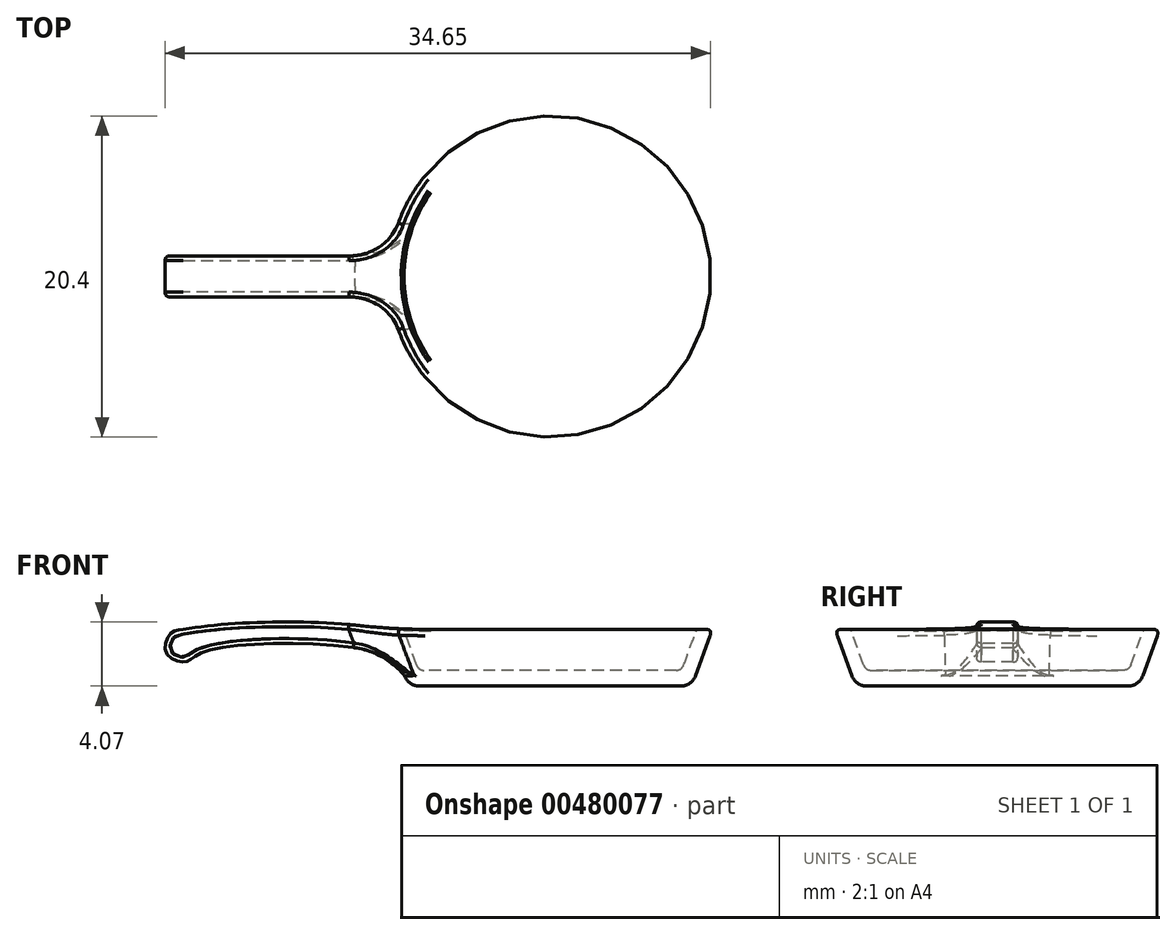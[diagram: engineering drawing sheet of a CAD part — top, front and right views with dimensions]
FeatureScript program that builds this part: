
annotation { "Feature Type Name" : "Feature", "Feature Type Description" : "" }
export const myFeature = defineFeature(function(context is Context, id is Id, definition is map)
    precondition{}
    {
        {
            var Q0;
            Q0=qCreatedBy(makeId("Top.planeOp"),FACE);
            var sketch = newSketch(context, id + "F0", { "sketchPlane" : qUnion([Q0])});
            skCircle(sketch, "E0", {"center": v(0, 0) * mm, "radius": 9 * mm});
            skSolve(sketch);
        }
        {
            var Q0;
            Q0 = qSketchRegion(id + "F0", true);
            extrude(context, id + "F1", {"entities" : qUnion([Q0]), "depth" : 1 * mm});
        }
        {
            var Q0;
            Q0=qCreatedBy(makeId("Front.planeOp"),FACE);
            var sketch = newSketch(context, id + "F2", { "sketchPlane" : qUnion([Q0])});
            skLineSegment(sketch, "E1.0.0", {"start": v(-8, 0) * mm, "end": v(-9, 0) * mm});
            skLineSegment(sketch, "E2", {"start": v(-9, 0) * mm, "end": v(-10.31, 3.6) * mm});
            skLineSegment(sketch, "E3", {"start": v(-10.31, 3.6) * mm, "end": v(-9.31, 3.6) * mm});
            skLineSegment(sketch, "E4", {"start": v(-9.31, 3.6) * mm, "end": v(-8, 0) * mm});
            skPoint(sketch, "E5.orphan", {"position": v(9, 0) * mm});
            skSolve(sketch);
        }
        {
            var Q0;
            Q0=makeQuery(id+"F2.imprint","IMPRINT",FACE,{"disambiguationData":[TD([[makeQuery(id+"F2.imprint","IMPRINT",EDGE,{"derivedFrom":sQuery(id+"F2.wireOp",EDGE,"E1.0.0")}),-1.0]])]});
            var Q1;
            Q1=makeQuery(id+"F1.opExtrude","CAP_EDGE",EDGE,{"disambiguationData":[OSD([sQuery(id+"F0.wireOp",EDGE,"E0")])],"isStart":true});
            revolve(context, id + "F3", {"operationType" : NewBodyOperationType.ADD, "entities" : qUnion([Q0]), "axis" : qUnion([Q1]), "revolveType" : RevolveType.FULL});
        }
        {
            var Q0;
            Q0=makeQuery(id+"F3.boolean.opBoolean","MERGE",EDGE,{"derivedFrom":[makeQuery(id+"F1.opExtrude","CAP_EDGE",EDGE,{"disambiguationData":[OSD([sQuery(id+"F0.wireOp",EDGE,"E0")])],"isStart":true}),makeQuery(id+"F3.opRevolve","SWEPT_EDGE",EDGE,{"disambiguationData":[OSD([sQuery(id+"F2.wireOp",EDGE,"E1.0.0"),sQuery(id+"F2.wireOp",EDGE,"E2")])]})]});
            fillet(context, id + "F4", {"entities" : qUnion([Q0]), "radius" : 1 * mm, "tangentPropagation" : true, "allowEdgeOverflow" : false});
        }
        {
            var Q0;
            Q0=makeQuery(id+"F3.boolean.opBoolean","INTERSECT",EDGE,{"derivedFrom":[makeQuery(id+"F1.opExtrude","CAP_FACE",FACE,{"disambiguationData":[OSD([sQuery(id+"F0.wireOp",EDGE,"E0")])],"isStart":false}),makeQuery(id+"F3.opRevolve","SWEPT_FACE",FACE,{"disambiguationData":[OSD([sQuery(id+"F2.wireOp",EDGE,"E4")])]})]});
            fillet(context, id + "F5", {"entities" : qUnion([Q0]), "radius" : .5 * mm, "tangentPropagation" : true, "allowEdgeOverflow" : false});
        }
        {
            var Q0;
            Q0=qCreatedBy(makeId("Front.planeOp"),FACE);
            var sketch = newSketch(context, id + "F6", { "sketchPlane" : qUnion([Q0])});
            skLineSegment(sketch, "E6.0", {"start": v(-9.44, 3.6) * mm, "end": v(-10.31, 3.6) * mm});
            skFitSpline(sketch, "E7", {"points": [v(-10.31, 3.6) * mm, v(-23.31, 3.6) * mm], "startDerivative": vector(-11.8, 2) * mm, "endDerivative": vector(-10.24, -1.77) * mm});
            skLineSegment(sketch, "E8", {"start": v(9.24, 0.66) * mm, "end": v(10.31, 3.6) * mm});
            skFitSpline(sketch, "E9", {"points": [v(-9.24, 1.7) * mm, v(-22.07, 2.14) * mm, v(-23.2, 1.53) * mm, v(-24.37, 2.1) * mm, v(-24.1, 3.34) * mm, v(-23.31, 3.6) * mm], "startDerivative": vector(-23.26, 8.79) * mm, "endDerivative": vector(7.3, 1.26) * mm});
            skLineSegment(sketch, "E10", {"start": v(-9.24, 1.7) * mm, "end": v(-9.44, 3.6) * mm});
            skPoint(sketch, "E11.end.orphan", {"position": v(-9.24, 0.66) * mm});
            skPoint(sketch, "E12.orphan", {"position": v(10.31, 3.6) * mm});
            skSolve(sketch);
        }
        {
            var Q0;
            Q0=makeQuery(id+"F6.imprint","IMPRINT",FACE,{"disambiguationData":[TD([[makeQuery(id+"F6.imprint","IMPRINT",EDGE,{"derivedFrom":sQuery(id+"F6.wireOp",EDGE,"E6.0")}),1.0]])]});
            extrude(context, id + "F7", {"entities" : qUnion([Q0]), "operationType" : NewBodyOperationType.ADD, "endBound" : BoundingType.SYMMETRIC, "depth" : 2.6 * mm});
        }
        {
            var Q0;
            Q0=makeQuery(id+"F7.boolean.opBoolean","INTERSECT",EDGE,{"derivedFrom":[makeQuery(id+"F3.opRevolve","SWEPT_FACE",FACE,{"disambiguationData":[OSD([sQuery(id+"F2.wireOp",EDGE,"E2")])]}),makeQuery(id+"F7.opExtrude","CAP_FACE",FACE,{"disambiguationData":[OSD([sQuery(id+"F6.wireOp",EDGE,"E6.0"),sQuery(id+"F6.wireOp",EDGE,"E7"),sQuery(id+"F6.wireOp",EDGE,"E9"),sQuery(id+"F6.wireOp",EDGE,"E10")])],"isStart":false})]});
            var Q1;
            Q1=makeQuery(id+"F7.boolean.opBoolean","INTERSECT",EDGE,{"derivedFrom":[makeQuery(id+"F3.opRevolve","SWEPT_FACE",FACE,{"disambiguationData":[OSD([sQuery(id+"F2.wireOp",EDGE,"E2")])]}),makeQuery(id+"F7.opExtrude","CAP_FACE",FACE,{"disambiguationData":[OSD([sQuery(id+"F6.wireOp",EDGE,"E6.0"),sQuery(id+"F6.wireOp",EDGE,"E7"),sQuery(id+"F6.wireOp",EDGE,"E9"),sQuery(id+"F6.wireOp",EDGE,"E10")])],"isStart":true})]});
            fillet(context, id + "F8", {"entities" : qUnion([Q0, Q1]), "radius" : 3 * mm, "tangentPropagation" : true, "allowEdgeOverflow" : false});
        }
        {
            var Q0;
            Q0=makeQuery(id+"F7.opExtrude","SWEPT_EDGE",EDGE,{"disambiguationData":[OSD([sQuery(id+"F6.wireOp",EDGE,"E6.0"),sQuery(id+"F6.wireOp",EDGE,"E7")])]});
            fillet(context, id + "F9", {"entities" : qUnion([Q0]), "radius" : 39.53 * mm, "tangentPropagation" : true, "allowEdgeOverflow" : false});
        }
        {
            var Q0;
            Q0=makeQuery(id+"F7.boolean.opBoolean","INTERSECT",EDGE,{"derivedFrom":[makeQuery(id+"F3.opRevolve","SWEPT_FACE",FACE,{"disambiguationData":[OSD([sQuery(id+"F2.wireOp",EDGE,"E2")])]}),makeQuery(id+"F7.opExtrude","SWEPT_FACE",FACE,{"disambiguationData":[OSD([sQuery(id+"F6.wireOp",EDGE,"E9")])]})]});
            fillet(context, id + "F10", {"entities" : qUnion([Q0]), "radius" : 5 * mm, "tangentPropagation" : true, "allowEdgeOverflow" : false});
        }
        {
            var Q0;
            {var subQ0=sQuery(id+"F6.wireOp",EDGE,"E10");var subQ1=sQuery(id+"F6.wireOp",EDGE,"E9");var subQ2=sQuery(id+"F6.wireOp",EDGE,"E7");var subQ3=sQuery(id+"F6.wireOp",EDGE,"E6.0");var subQ4=sQuery(id+"F2.wireOp",EDGE,"E2");var subQ5=makeQuery(id+"F3.opRevolve","SWEPT_FACE",FACE,{"disambiguationData":[OSD([subQ4])]});Q0=makeQuery(id+"F10.opFillet","BLEND_EDGE",EDGE,{"blendedFrom":[makeQuery(id+"F7.boolean.opBoolean","INTERSECT",EDGE,{"derivedFrom":[subQ5,makeQuery(id+"F7.opExtrude","SWEPT_FACE",FACE,{"disambiguationData":[OSD([subQ1])]})]}),makeQuery(id+"F8.opFillet","BLEND_FACE",FACE,{"disambiguationData":[OSD([subQ4,subQ3,subQ2,subQ1,subQ0]),TDD([makeQuery(id+"F7.boolean.opBoolean","INTERSECT",EDGE,{"derivedFrom":[subQ5,makeQuery(id+"F7.opExtrude","CAP_FACE",FACE,{"disambiguationData":[OSD([subQ3,subQ2,subQ1,subQ0])],"isStart":false})]})])]})],"blendedInto":[makeQuery(id+"F8.opFillet","BLEND_FACE",FACE,{"disambiguationData":[OSD([subQ4,subQ3,subQ2,subQ1,subQ0]),TDD([makeQuery(id+"F7.boolean.opBoolean","INTERSECT",EDGE,{"derivedFrom":[subQ5,makeQuery(id+"F7.opExtrude","CAP_FACE",FACE,{"disambiguationData":[OSD([subQ3,subQ2,subQ1,subQ0])],"isStart":false})]})])]})]});}
            var Q1;
            {var subQ0=sQuery(id+"F6.wireOp",EDGE,"E10");var subQ1=sQuery(id+"F6.wireOp",EDGE,"E9");var subQ2=sQuery(id+"F6.wireOp",EDGE,"E7");var subQ3=sQuery(id+"F6.wireOp",EDGE,"E6.0");var subQ4=sQuery(id+"F2.wireOp",EDGE,"E2");var subQ5=makeQuery(id+"F3.opRevolve","SWEPT_FACE",FACE,{"disambiguationData":[OSD([subQ4])]});Q1=makeQuery(id+"F10.opFillet","BLEND_EDGE",EDGE,{"blendedFrom":[makeQuery(id+"F7.boolean.opBoolean","INTERSECT",EDGE,{"derivedFrom":[subQ5,makeQuery(id+"F7.opExtrude","SWEPT_FACE",FACE,{"disambiguationData":[OSD([subQ1])]})]}),makeQuery(id+"F8.opFillet","BLEND_FACE",FACE,{"disambiguationData":[OSD([subQ4,subQ3,subQ2,subQ1,subQ0]),TDD([makeQuery(id+"F7.boolean.opBoolean","INTERSECT",EDGE,{"derivedFrom":[subQ5,makeQuery(id+"F7.opExtrude","CAP_FACE",FACE,{"disambiguationData":[OSD([subQ3,subQ2,subQ1,subQ0])],"isStart":true})]})])]})],"blendedInto":[makeQuery(id+"F8.opFillet","BLEND_FACE",FACE,{"disambiguationData":[OSD([subQ4,subQ3,subQ2,subQ1,subQ0]),TDD([makeQuery(id+"F7.boolean.opBoolean","INTERSECT",EDGE,{"derivedFrom":[subQ5,makeQuery(id+"F7.opExtrude","CAP_FACE",FACE,{"disambiguationData":[OSD([subQ3,subQ2,subQ1,subQ0])],"isStart":true})]})])]})]});}
            var Q2;
            Q2=makeQuery(id+"F7.opExtrude","CAP_EDGE",EDGE,{"disambiguationData":[OSD([sQuery(id+"F6.wireOp",EDGE,"E9")])],"isStart":true});
            var Q3;
            Q3=makeQuery(id+"F7.opExtrude","CAP_EDGE",EDGE,{"disambiguationData":[OSD([sQuery(id+"F6.wireOp",EDGE,"E7")])],"isStart":true});
            var Q4;
            {var subQ0=sQuery(id+"F6.wireOp",EDGE,"E10");var subQ1=sQuery(id+"F6.wireOp",EDGE,"E9");var subQ2=sQuery(id+"F6.wireOp",EDGE,"E7");var subQ3=sQuery(id+"F6.wireOp",EDGE,"E6.0");var subQ4=sQuery(id+"F2.wireOp",EDGE,"E2");Q4=makeQuery(id+"F9.opFillet","BLEND_EDGE",EDGE,{"blendedFrom":[makeQuery(id+"F7.opExtrude","SWEPT_EDGE",EDGE,{"disambiguationData":[OSD([subQ3,subQ2])]}),makeQuery(id+"F8.opFillet","BLEND_FACE",FACE,{"disambiguationData":[OSD([subQ4,subQ3,subQ2,subQ1,subQ0]),TDD([makeQuery(id+"F7.boolean.opBoolean","INTERSECT",EDGE,{"derivedFrom":[makeQuery(id+"F3.opRevolve","SWEPT_FACE",FACE,{"disambiguationData":[OSD([subQ4])]}),makeQuery(id+"F7.opExtrude","CAP_FACE",FACE,{"disambiguationData":[OSD([subQ3,subQ2,subQ1,subQ0])],"isStart":true})]})])]})],"blendedInto":[makeQuery(id+"F8.opFillet","BLEND_FACE",FACE,{"disambiguationData":[OSD([subQ4,subQ3,subQ2,subQ1,subQ0]),TDD([makeQuery(id+"F7.boolean.opBoolean","INTERSECT",EDGE,{"derivedFrom":[makeQuery(id+"F3.opRevolve","SWEPT_FACE",FACE,{"disambiguationData":[OSD([subQ4])]}),makeQuery(id+"F7.opExtrude","CAP_FACE",FACE,{"disambiguationData":[OSD([subQ3,subQ2,subQ1,subQ0])],"isStart":true})]})])]})]});}
            var Q5;
            {var subQ0=sQuery(id+"F6.wireOp",EDGE,"E7");Q5=makeQuery(id+"F8.opFillet","BLEND_EDGE",EDGE,{"blendedFrom":[makeQuery(id+"F7.boolean.opBoolean","INTERSECT",EDGE,{"derivedFrom":[makeQuery(id+"F3.opRevolve","SWEPT_FACE",FACE,{"disambiguationData":[OSD([sQuery(id+"F2.wireOp",EDGE,"E2")])]}),makeQuery(id+"F7.opExtrude","CAP_FACE",FACE,{"disambiguationData":[OSD([sQuery(id+"F6.wireOp",EDGE,"E6.0"),subQ0,sQuery(id+"F6.wireOp",EDGE,"E9"),sQuery(id+"F6.wireOp",EDGE,"E10")])],"isStart":true})]}),makeQuery(id+"F7.opExtrude","SWEPT_FACE",FACE,{"disambiguationData":[OSD([subQ0])]})],"blendedInto":[makeQuery(id+"F7.opExtrude","SWEPT_FACE",FACE,{"disambiguationData":[OSD([subQ0])]})]});}
            var Q6;
            {var subQ0=sQuery(id+"F6.wireOp",EDGE,"E10");var subQ1=sQuery(id+"F6.wireOp",EDGE,"E9");var subQ2=sQuery(id+"F6.wireOp",EDGE,"E7");var subQ3=sQuery(id+"F6.wireOp",EDGE,"E6.0");var subQ4=sQuery(id+"F2.wireOp",EDGE,"E2");Q6=makeQuery(id+"F9.opFillet","BLEND_EDGE",EDGE,{"blendedFrom":[makeQuery(id+"F7.opExtrude","SWEPT_EDGE",EDGE,{"disambiguationData":[OSD([subQ3,subQ2])]}),makeQuery(id+"F8.opFillet","BLEND_FACE",FACE,{"disambiguationData":[OSD([subQ4,subQ3,subQ2,subQ1,subQ0]),TDD([makeQuery(id+"F7.boolean.opBoolean","INTERSECT",EDGE,{"derivedFrom":[makeQuery(id+"F3.opRevolve","SWEPT_FACE",FACE,{"disambiguationData":[OSD([subQ4])]}),makeQuery(id+"F7.opExtrude","CAP_FACE",FACE,{"disambiguationData":[OSD([subQ3,subQ2,subQ1,subQ0])],"isStart":false})]})])]})],"blendedInto":[makeQuery(id+"F8.opFillet","BLEND_FACE",FACE,{"disambiguationData":[OSD([subQ4,subQ3,subQ2,subQ1,subQ0]),TDD([makeQuery(id+"F7.boolean.opBoolean","INTERSECT",EDGE,{"derivedFrom":[makeQuery(id+"F3.opRevolve","SWEPT_FACE",FACE,{"disambiguationData":[OSD([subQ4])]}),makeQuery(id+"F7.opExtrude","CAP_FACE",FACE,{"disambiguationData":[OSD([subQ3,subQ2,subQ1,subQ0])],"isStart":false})]})])]})]});}
            var Q7;
            {var subQ0=sQuery(id+"F6.wireOp",EDGE,"E7");Q7=makeQuery(id+"F8.opFillet","BLEND_EDGE",EDGE,{"blendedFrom":[makeQuery(id+"F7.boolean.opBoolean","INTERSECT",EDGE,{"derivedFrom":[makeQuery(id+"F3.opRevolve","SWEPT_FACE",FACE,{"disambiguationData":[OSD([sQuery(id+"F2.wireOp",EDGE,"E2")])]}),makeQuery(id+"F7.opExtrude","CAP_FACE",FACE,{"disambiguationData":[OSD([sQuery(id+"F6.wireOp",EDGE,"E6.0"),subQ0,sQuery(id+"F6.wireOp",EDGE,"E9"),sQuery(id+"F6.wireOp",EDGE,"E10")])],"isStart":false})]}),makeQuery(id+"F7.opExtrude","SWEPT_FACE",FACE,{"disambiguationData":[OSD([subQ0])]})],"blendedInto":[makeQuery(id+"F7.opExtrude","SWEPT_FACE",FACE,{"disambiguationData":[OSD([subQ0])]})]});}
            var Q8;
            Q8=makeQuery(id+"F7.opExtrude","CAP_EDGE",EDGE,{"disambiguationData":[OSD([sQuery(id+"F6.wireOp",EDGE,"E7")])],"isStart":false});
            var Q9;
            Q9=makeQuery(id+"F7.opExtrude","CAP_EDGE",EDGE,{"disambiguationData":[OSD([sQuery(id+"F6.wireOp",EDGE,"E9")])],"isStart":false});
            var Q10;
            Q10=makeQuery(id+"F9.opFillet","BLEND_EDGE",EDGE,{"disambiguationData":[OD(1.0)],"blendedFrom":[makeQuery(id+"F7.opExtrude","SWEPT_EDGE",EDGE,{"disambiguationData":[OSD([sQuery(id+"F6.wireOp",EDGE,"E6.0"),sQuery(id+"F6.wireOp",EDGE,"E7")])]}),makeQuery(id+"F3.opRevolve","SWEPT_FACE",FACE,{"disambiguationData":[OSD([sQuery(id+"F2.wireOp",EDGE,"E2")])]})],"blendedInto":[makeQuery(id+"F3.opRevolve","SWEPT_FACE",FACE,{"disambiguationData":[OSD([sQuery(id+"F2.wireOp",EDGE,"E2")])]})]});
            var Q11;
            Q11=makeQuery(id+"F3.opRevolve","SWEPT_EDGE",EDGE,{"disambiguationData":[OSD([sQuery(id+"F2.wireOp",EDGE,"E2"),sQuery(id+"F2.wireOp",EDGE,"E3")])]});
            var Q12;
            Q12=makeQuery(id+"F9.opFillet","BLEND_EDGE",EDGE,{"disambiguationData":[OD(0.0)],"blendedFrom":[makeQuery(id+"F7.opExtrude","SWEPT_EDGE",EDGE,{"disambiguationData":[OSD([sQuery(id+"F6.wireOp",EDGE,"E6.0"),sQuery(id+"F6.wireOp",EDGE,"E7")])]}),makeQuery(id+"F3.opRevolve","SWEPT_FACE",FACE,{"disambiguationData":[OSD([sQuery(id+"F2.wireOp",EDGE,"E2")])]})],"blendedInto":[makeQuery(id+"F3.opRevolve","SWEPT_FACE",FACE,{"disambiguationData":[OSD([sQuery(id+"F2.wireOp",EDGE,"E2")])]})]});
            fillet(context, id + "F11", {"entities" : qUnion([Q0, Q1, Q2, Q3, Q4, Q5, Q6, Q7, Q8, Q9, Q10, Q11, Q12]), "radius" : .3 * mm, "rho" : .5, "crossSection" : FilletCrossSection.CONIC, "allowEdgeOverflow" : false});
        }
        {
            var Q0;
            Q0=makeQuery(id+"F3.opRevolve","SWEPT_EDGE",EDGE,{"disambiguationData":[OSD([sQuery(id+"F2.wireOp",EDGE,"E3"),sQuery(id+"F2.wireOp",EDGE,"E4")])]});
            var Q1;
            Q1=makeQuery(id+"F9.opFillet","BLEND_EDGE",EDGE,{"blendedFrom":[makeQuery(id+"F7.opExtrude","SWEPT_EDGE",EDGE,{"disambiguationData":[OSD([sQuery(id+"F6.wireOp",EDGE,"E6.0"),sQuery(id+"F6.wireOp",EDGE,"E7")])]}),makeQuery(id+"F3.opRevolve","SWEPT_FACE",FACE,{"disambiguationData":[OSD([sQuery(id+"F2.wireOp",EDGE,"E4")])]})],"blendedInto":[makeQuery(id+"F3.opRevolve","SWEPT_FACE",FACE,{"disambiguationData":[OSD([sQuery(id+"F2.wireOp",EDGE,"E4")])]})]});
            fillet(context, id + "F12", {"entities" : qUnion([Q0, Q1]), "radius" : .2 * mm, "tangentPropagation" : true, "allowEdgeOverflow" : false});
        }
    });
